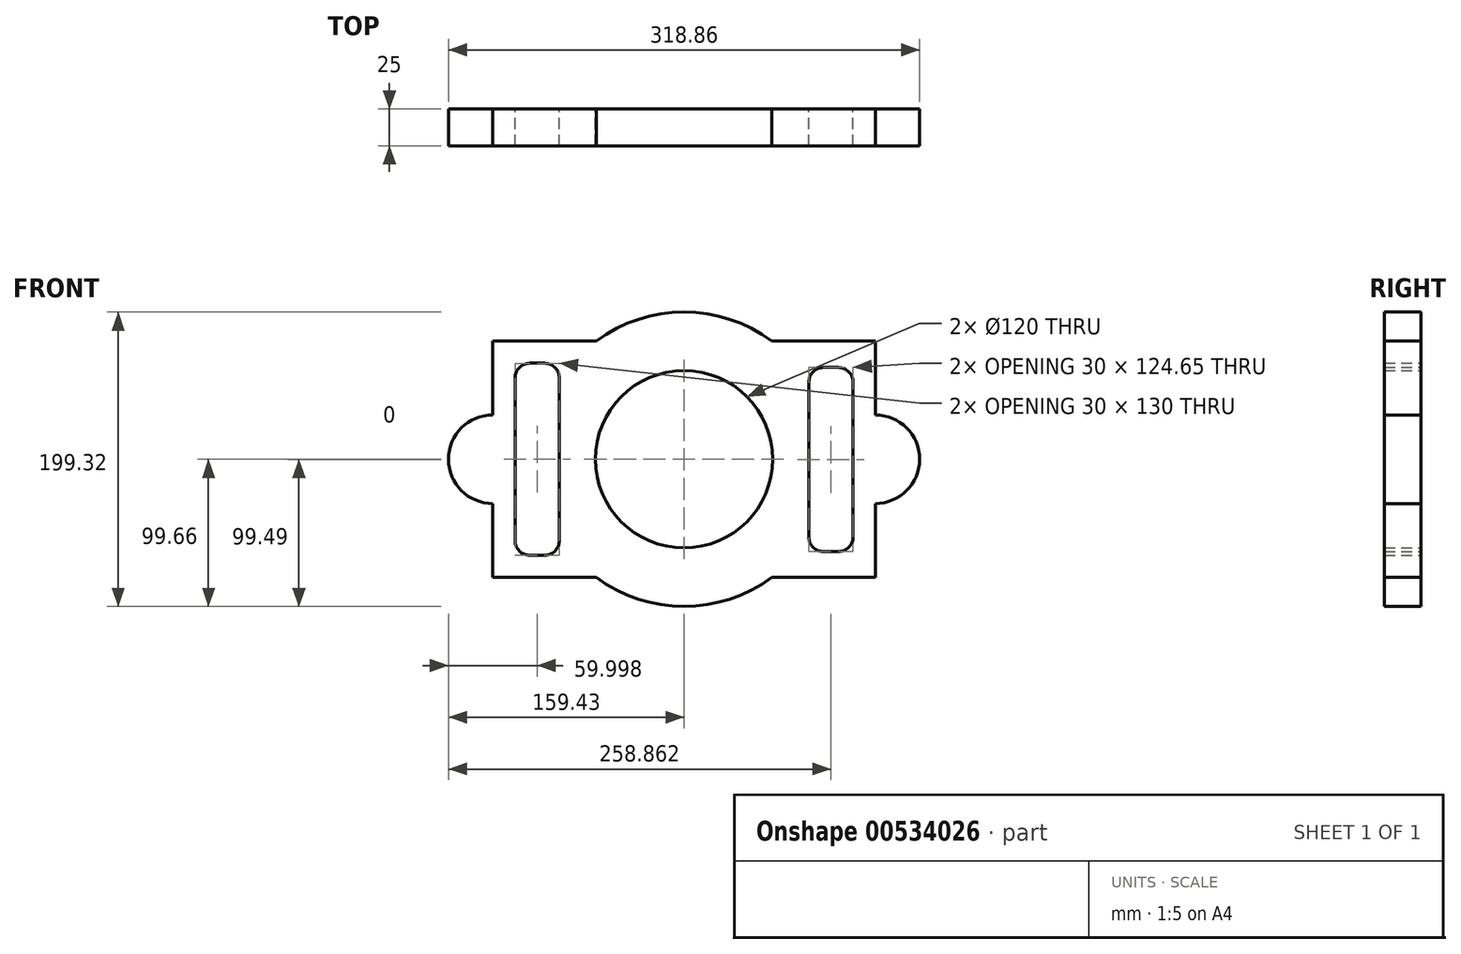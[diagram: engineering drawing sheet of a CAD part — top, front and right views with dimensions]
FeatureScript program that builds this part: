
annotation { "Feature Type Name" : "Feature", "Feature Type Description" : "" }
export const myFeature = defineFeature(function(context is Context, id is Id, definition is map)
    precondition{}
    {
        {
            var Q0;
            Q0=qCreatedBy(makeId("Front.planeOp"),FACE);
            var sketch = newSketch(context, id + "F0", { "sketchPlane" : qUnion([Q0])});
            skCircle(sketch, "E0", {"center": v(0, 0) * mm, "radius": 60 * mm});
            skLineSegment(sketch, "E1", {"start": v(0, 0) * mm, "end": v(60, 0) * mm});
            skLineSegment(sketch, "E2.left", {"start": v(-129.43, 80) * mm, "end": v(-129.43, 30) * mm});
            skLineSegment(sketch, "E2.right", {"start": v(129.43, 80) * mm, "end": v(129.43, 30) * mm});
            skArc(sketch, "E3", {"start": v(-59.43, -80) * mm, "mid": v(0, -99.66) * mm, "end": v(59.43, -80) * mm});
            skLineSegment(sketch, "E4", {"start": v(0, 0) * mm, "end": v(0, 60) * mm});
            skLineSegment(sketch, "E5", {"start": v(-129.43, 80) * mm, "end": v(-59.43, 80) * mm});
            skLineSegment(sketch, "E6", {"start": v(129.43, 80) * mm, "end": v(59.43, 80) * mm});
            skLineSegment(sketch, "E7", {"start": v(-129.43, -80) * mm, "end": v(-59.43, -80) * mm});
            skLineSegment(sketch, "E8", {"start": v(129.43, -80) * mm, "end": v(59.43, -80) * mm});
            skArc(sketch, "E9", {"start": v(-129.43, 30) * mm, "mid": v(-159.43, 0) * mm, "end": v(-129.43, -30) * mm});
            skArc(sketch, "E10", {"start": v(129.43, -30) * mm, "mid": v(159.43, 0) * mm, "end": v(129.43, 30) * mm});
            skLineSegment(sketch, "E11.bottom", {"start": v(-104.43, 65) * mm, "end": v(-94.43, 65) * mm});
            skLineSegment(sketch, "E11.top", {"start": v(-104.43, -65) * mm, "end": v(-94.43, -65) * mm});
            skLineSegment(sketch, "E11.left", {"start": v(-114.43, 55) * mm, "end": v(-114.43, -55) * mm});
            skLineSegment(sketch, "E11.right", {"start": v(-84.43, 55) * mm, "end": v(-84.43, -55) * mm});
            skArc(sketch, "E12.trimOffspring", {"start": v(59.43, 80) * mm, "mid": v(0, 99.66) * mm, "end": v(-59.43, 80) * mm});
            skLineSegment(sketch, "E13.trimOffspring", {"start": v(-129.43, -30) * mm, "end": v(-129.43, -80) * mm});
            skLineSegment(sketch, "E14.trimOffspring", {"start": v(129.43, -30) * mm, "end": v(129.43, -80) * mm});
            skPoint(sketch, "E15.visualSharp", {"position": v(-114.43, -65) * mm});
            skArc(sketch, "E15.filletArc", {"start": v(-114.43, -55) * mm, "mid": v(-111.5, -62.07) * mm, "end": v(-104.43, -65) * mm});
            skPoint(sketch, "E16.visualSharp", {"position": v(-84.43, -65) * mm});
            skArc(sketch, "E16.filletArc", {"start": v(-94.43, -65) * mm, "mid": v(-87.36, -62.07) * mm, "end": v(-84.43, -55) * mm});
            skPoint(sketch, "E17.visualSharp", {"position": v(-114.43, 65) * mm});
            skArc(sketch, "E17.filletArc", {"start": v(-104.43, 65) * mm, "mid": v(-111.5, 62.07) * mm, "end": v(-114.43, 55) * mm});
            skPoint(sketch, "E18.visualSharp", {"position": v(-84.43, 65) * mm});
            skArc(sketch, "E18.filletArc", {"start": v(-84.43, 55) * mm, "mid": v(-87.36, 62.07) * mm, "end": v(-94.43, 65) * mm});
            skLineSegment(sketch, "E19", {"start": v(0, 0) * mm, "end": v(-84.43, 0) * mm});
            skLineSegment(sketch, "E20.bottom", {"start": v(94.43, 62.15) * mm, "end": v(104.43, 62.15) * mm});
            skLineSegment(sketch, "E20.top", {"start": v(94.43, -62.5) * mm, "end": v(104.43, -62.5) * mm});
            skLineSegment(sketch, "E20.left", {"start": v(84.43, 52.15) * mm, "end": v(84.43, -52.5) * mm});
            skLineSegment(sketch, "E20.right", {"start": v(114.43, 52.15) * mm, "end": v(114.43, -52.5) * mm});
            skLineSegment(sketch, "E21", {"start": v(0, 0) * mm, "end": v(84.43, 0) * mm});
            skPoint(sketch, "E22.visualSharp", {"position": v(84.43, -62.5) * mm});
            skArc(sketch, "E22.filletArc", {"start": v(84.43, -52.5) * mm, "mid": v(87.36, -59.57) * mm, "end": v(94.43, -62.5) * mm});
            skPoint(sketch, "E23.visualSharp", {"position": v(114.43, -62.5) * mm});
            skArc(sketch, "E23.filletArc", {"start": v(104.43, -62.5) * mm, "mid": v(111.5, -59.57) * mm, "end": v(114.43, -52.5) * mm});
            skPoint(sketch, "E24.visualSharp", {"position": v(84.43, 62.15) * mm});
            skArc(sketch, "E24.filletArc", {"start": v(94.43, 62.15) * mm, "mid": v(87.36, 59.23) * mm, "end": v(84.43, 52.15) * mm});
            skPoint(sketch, "E25.visualSharp", {"position": v(114.43, 62.15) * mm});
            skArc(sketch, "E25.filletArc", {"start": v(114.43, 52.15) * mm, "mid": v(111.5, 59.23) * mm, "end": v(104.43, 62.15) * mm});
            skSolve(sketch);
        }
        {
            var Q0;
            Q0=makeQuery(id+"F0.imprint","IMPRINT",FACE,{"disambiguationData":[TD([[makeQuery(id+"F0.imprint","IMPRINT",EDGE,{"derivedFrom":sQuery(id+"F0.wireOp",EDGE,"E2.left")}),1.0]])]});
            extrude(context, id + "F1", {"entities" : qUnion([Q0]), "depth" : 25 * mm, "offsetDistance" : 25 * mm});
        }
    });
